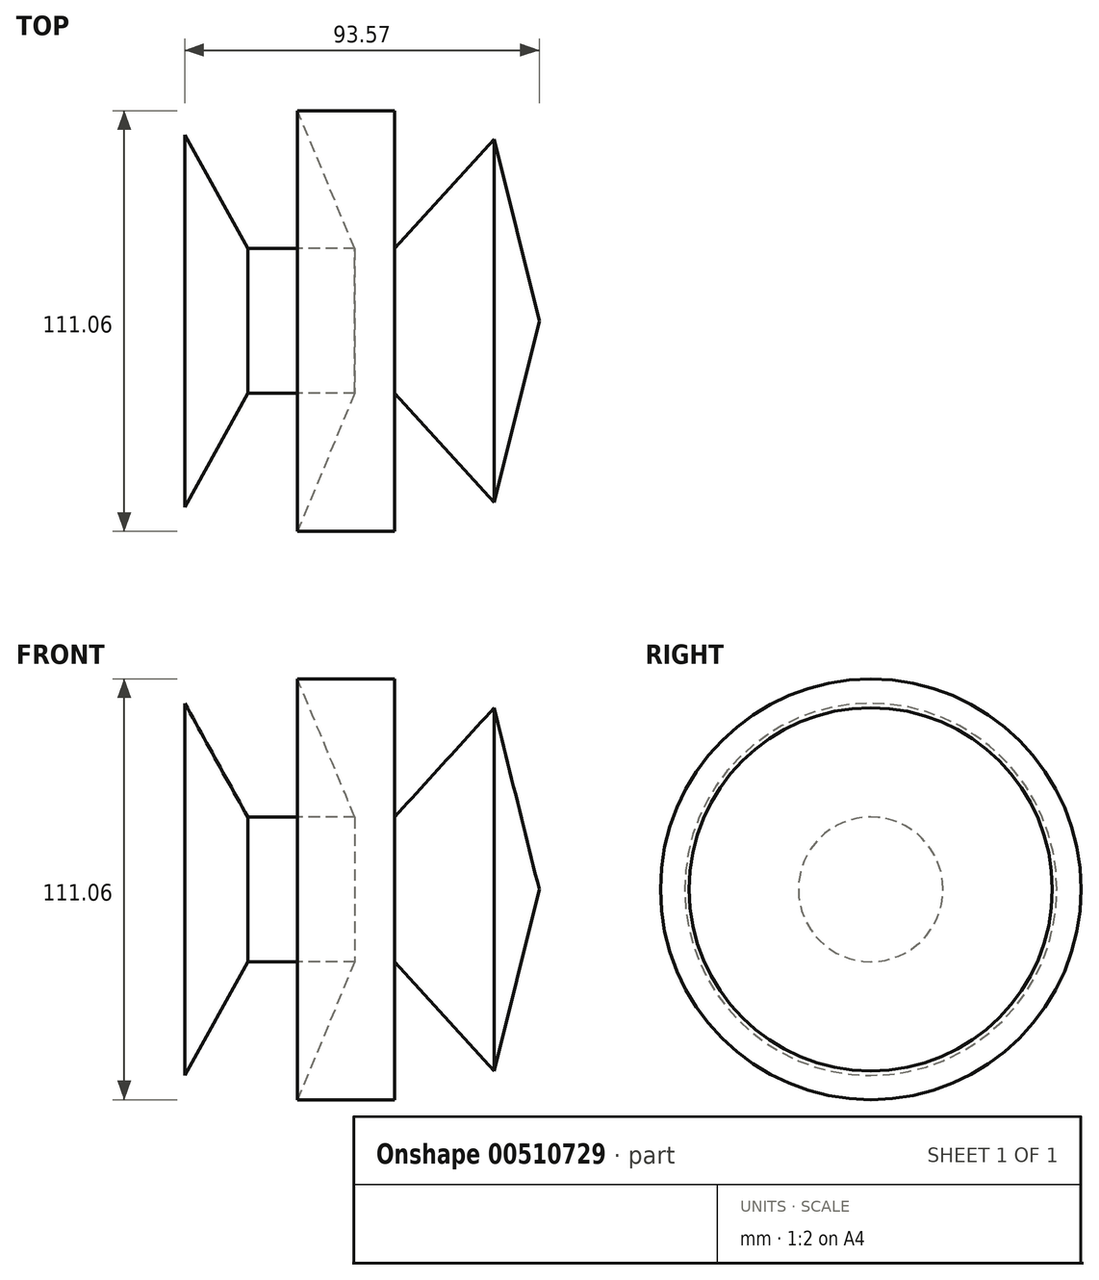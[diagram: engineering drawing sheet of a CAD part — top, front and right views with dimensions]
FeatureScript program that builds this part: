
annotation { "Feature Type Name" : "Feature", "Feature Type Description" : "" }
export const myFeature = defineFeature(function(context is Context, id is Id, definition is map)
    precondition{}
    {
        {
            var Q0;
            Q0=qCreatedBy(makeId("Top.planeOp"),FACE);
            var sketch = newSketch(context, id + "F0", { "sketchPlane" : qUnion([Q0])});
            skLineSegment(sketch, "E0", {"start": v(-45.47, 0) * mm, "end": v(48.68, 0) * mm});
            skLineSegment(sketch, "E1", {"start": v(48.68, 0) * mm, "end": v(36.73, -47.95) * mm});
            skLineSegment(sketch, "E2", {"start": v(36.73, -47.95) * mm, "end": v(10.5, -19.1) * mm});
            skLineSegment(sketch, "E3", {"start": v(10.5, -19.1) * mm, "end": v(10.5, -55.53) * mm});
            skLineSegment(sketch, "E4", {"start": v(10.5, -55.53) * mm, "end": v(-15.16, -55.53) * mm});
            skLineSegment(sketch, "E5", {"start": v(-15.16, -55.53) * mm, "end": v(0, -19.1) * mm});
            skLineSegment(sketch, "E6", {"start": v(0, -19.1) * mm, "end": v(-28.27, -19.1) * mm});
            skLineSegment(sketch, "E7", {"start": v(-28.27, -19.1) * mm, "end": v(-44.89, -49.11) * mm});
            skLineSegment(sketch, "E8", {"start": v(-44.89, -49.11) * mm, "end": v(-44.89, 0) * mm});
            skSolve(sketch);
        }
        {
            var Q0;
            {var subQ0=sQuery(id+"F0.wireOp",EDGE,"E1");Q0=makeQuery(id+"F0.imprint","IMPRINT",FACE,{"disambiguationData":[TD([[makeQuery(id+"F0.imprint","IMPRINT",EDGE,{"derivedFrom":subQ0}),-1.0]])]});}
            var Q1;
            Q1=sQuery(id+"F0.wireOp",EDGE,"E0");
            revolve(context, id + "F1", {"entities" : qUnion([Q0]), "axis" : qUnion([Q1]), "revolveType" : RevolveType.FULL});
        }
    });
